AUTODESK INVENTOR PART (.ipt)
format: ipt  version: 2017 (Build 210142000, 142)  size: 502,784 bytes
history: native  units: mm
features: other x24, loft x2, pattern_circular x2, sketch x2
ambient origin geometry x6: Origin, XZ Plane, X Axis, Y Axis, Z Axis, Center Point
bodies: Solid1 (feature_tree)
feature tree (30):
  other  "Top Point"
  other  "Mesh Plane2"
  other  "Teeth Body"
  other  "Start Point"
  other  "Tooth Plane"
  other  "Start Sketch"
  other  "End Point"
  other  "3D Sketch Right"
  other  "End Plane Right"
  loft  "Loft Right"
  pattern_circular  "Circular Pattern Right"  [2 undecoded]
  other  "3D Sketch Left"
  other  "End Plane Left"
  loft  "Loft Left"
  pattern_circular  "Circular Pattern Left"  Angle=90.0deg  [1 undecoded]
  other  "Fix Body"
  sketch  "Sketch8"  dims[d2=42.951742mm d3=7.62mm d4=154.641737mm d5=90.0deg d7=7.255814mm d8=8.463759mm d9=15.810481mm d11=7.894607mm d12=6.89613mm d15=8.044195mm d16=15.026726mm d17=0.0mm d18=90.0deg d19=0.0mm d20=90.0deg d21=150.0mm d22=360.0deg d26=314.208686mm d27=7.835604mm d28=38.1mm d29=-1.223368mm d30=6.89613mm d31=8.044195mm d32=15.026726mm d35=0.0mm d37=0.0mm d39=0.0mm d40=90.0deg d41=150.0mm d42=360.0deg d46=90.0deg d47=90.0deg d48=0.0mm d49=0.0mm d50=90.0deg d51=2.094395mm d52=0.0mm d53=0.0mm d54=0.0mm d56=20.274923mm d57=23.285228mm d58=15.486392mm d59=22.130936mm d60=14.718703mm d61=22.130936mm d62=14.718703mm d63=90.0deg d64=90.0deg d65=314.208686mm d66=31.5mm d67=38.1mm d68=-1.223368mm d69=7.835604mm d70=8.044195mm d71=15.026726mm d72=6.89613mm d73=14.718703mm d74=22.130936mm d75=0.0mm d76=90.0deg d77=0.0mm d78=90.0deg d79=0.0mm d80=90.0deg d81=150.0mm d82=360.0deg d84=10.0mm d85=20.0mm d86=20.0mm d87=10.0mm d88=0.0mm d89=0.0mm]
  other  "Mesh Plane"
  other  "Top Plane"
  other  "Teeth Body Sketch"
  other  "End Plane"
  other  "End Sketch"
  other  "Helical Curve Left"
  other  "End Sketch Left"
  other  "Body Sketch"
  sketch  "Sketch6"  dims[d0=38.1mm d1=32.04956mm]
  other  "Srf1"
  other  "Helical Curve Right"
  other  "End Sketch Right"
  other  "Pitch Diameter"
note: 3 required parameter values undecoded (feature->parameter linkage not recoverable at this tier; creation-order binding heuristic only, values carry confidence <= 0.55)
